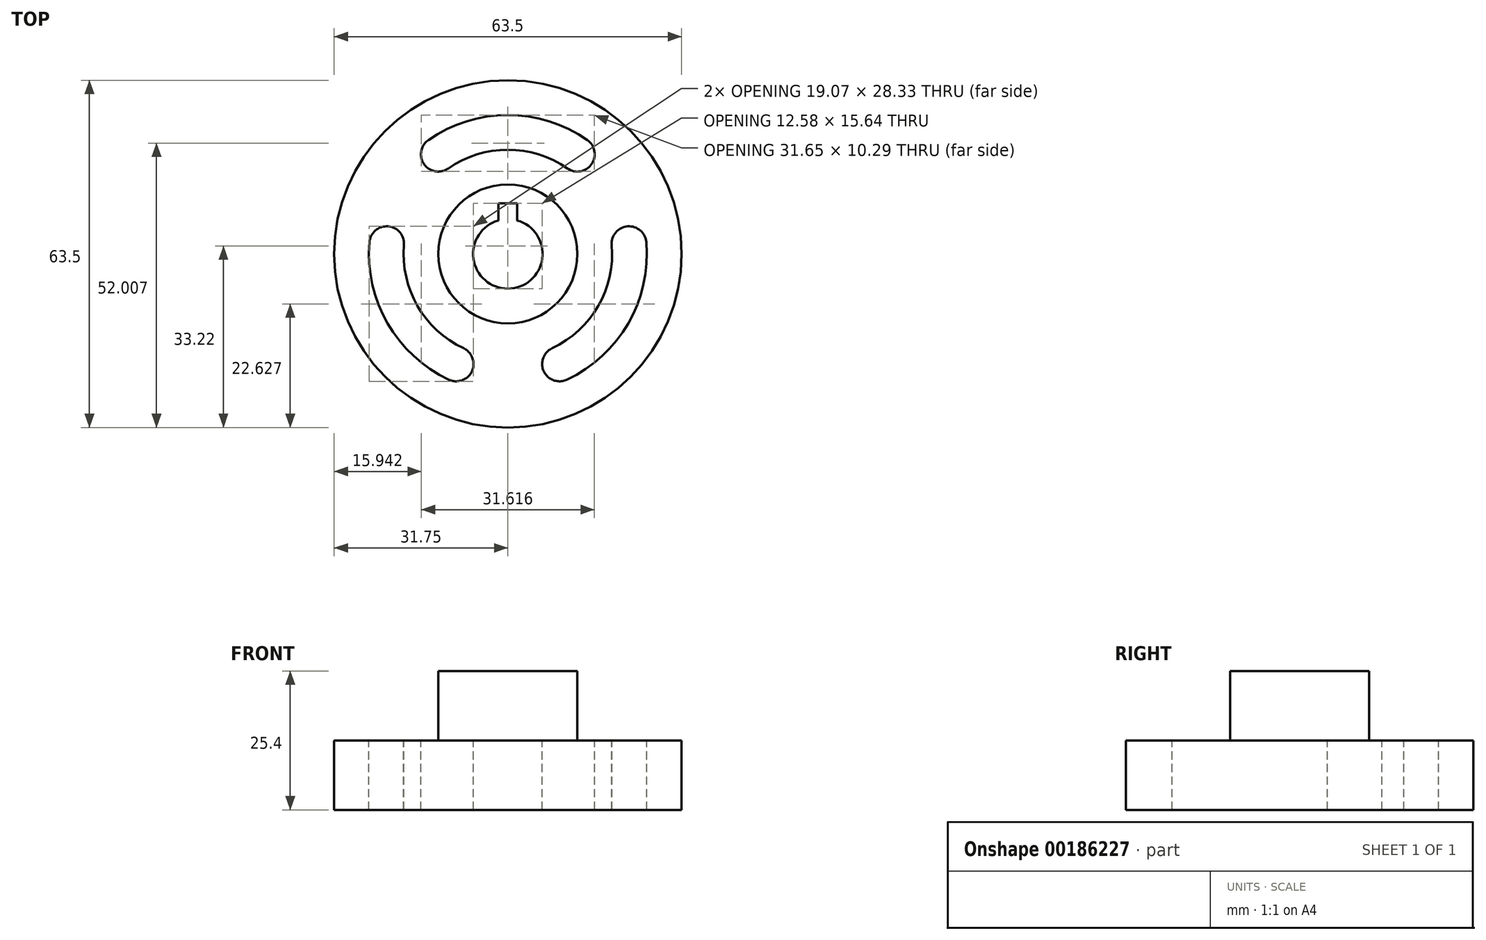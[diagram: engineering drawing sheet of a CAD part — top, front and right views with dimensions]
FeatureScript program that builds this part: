
annotation { "Feature Type Name" : "Feature", "Feature Type Description" : "" }
export const myFeature = defineFeature(function(context is Context, id is Id, definition is map)
    precondition{}
    {
        {
            var Q0;
            Q0=qCreatedBy(makeId("Top.planeOp"),FACE);
            var sketch = newSketch(context, id + "F0", { "sketchPlane" : qUnion([Q0])});
            skArc(sketch, "E0", {"start": v(-1.71, 6.11) * mm, "mid": v(0, -6.35) * mm, "end": v(1.71, 6.11) * mm});
            skCircle(sketch, "E1", {"center": v(0, 0) * mm, "radius": 12.7 * mm});
            skLineSegment(sketch, "E2.top", {"start": v(-1.71, 9.29) * mm, "end": v(1.71, 9.29) * mm});
            skLineSegment(sketch, "E2.left", {"start": v(-1.71, 6.11) * mm, "end": v(-1.71, 9.29) * mm});
            skLineSegment(sketch, "E2.right", {"start": v(1.71, 6.11) * mm, "end": v(1.71, 9.29) * mm});
            skLineSegment(sketch, "E3", {"start": v(0, 9.29) * mm, "end": v(0, 0) * mm, "construction": true});
            skSolve(sketch);
        }
        {
            var Q0;
            Q0=makeQuery(id+"F0.imprint","IMPRINT",FACE,{"disambiguationData":[TD([[makeQuery(id+"F0.imprint","IMPRINT",EDGE,{"derivedFrom":sQuery(id+"F0.wireOp",EDGE,"E0")}),-1.0]])]});
            extrude(context, id + "F1", {"entities" : qUnion([Q0]), "depth" : 25.4 * mm});
        }
        {
            var Q0;
            Q0=makeQuery(id+"F1.opExtrude","CAP_FACE",FACE,{"disambiguationData":[OSD([sQuery(id+"F0.wireOp",EDGE,"E0"),sQuery(id+"F0.wireOp",EDGE,"E1"),sQuery(id+"F0.wireOp",EDGE,"E2.top"),sQuery(id+"F0.wireOp",EDGE,"E2.left"),sQuery(id+"F0.wireOp",EDGE,"E2.right")])],"isStart":true});
            var sketch = newSketch(context, id + "F2", { "sketchPlane" : qUnion([Q0])});
            skCircle(sketch, "E4", {"center": v(0, 0) * mm, "radius": 31.75 * mm});
            skCircle(sketch, "E5.0", {"center": v(0, 0) * mm, "radius": 12.7 * mm});
            skSolve(sketch);
        }
        {
            var Q0;
            Q0=makeQuery(id+"F2.imprint","IMPRINT",FACE,{"disambiguationData":[TD([[makeQuery(id+"F2.imprint","IMPRINT",EDGE,{"derivedFrom":sQuery(id+"F2.wireOp",EDGE,"E4")}),1.0]])]});
            extrude(context, id + "F3", {"entities" : qUnion([Q0]), "operationType" : NewBodyOperationType.ADD, "oppositeDirection" : true, "depth" : 12.7 * mm});
        }
        {
            var Q0;
            Q0=makeQuery(id+"F3.opExtrude","CAP_FACE",FACE,{"disambiguationData":[OSD([sQuery(id+"F2.wireOp",EDGE,"E4"),sQuery(id+"F2.wireOp",EDGE,"E5.0")])],"isStart":false});
            var sketch = newSketch(context, id + "F4", { "sketchPlane" : qUnion([Q0])});
            skCircle(sketch, "E6.0", {"center": v(0, 0) * mm, "radius": 12.7 * mm, "construction": true});
            skLineSegment(sketch, "E7", {"start": v(0, 31.75) * mm, "end": v(0, 12.7) * mm, "construction": true});
            skLineSegment(sketch, "E8", {"start": v(0, -12.7) * mm, "end": v(0, -31.75) * mm});
            skArc(sketch, "E9", {"start": v(-12.7, 18.24) * mm, "mid": v(0, 22.23) * mm, "end": v(12.7, 18.24) * mm});
            skArc(sketch, "E10.0.startCap", {"start": v(-10.89, 15.63) * mm, "mid": v(-15.3, 16.42) * mm, "end": v(-14.51, 20.84) * mm});
            skArc(sketch, "E10.0.endCap", {"start": v(14.51, 20.84) * mm, "mid": v(15.3, 16.42) * mm, "end": v(10.89, 15.63) * mm});
            skArc(sketch, "E10.0.left", {"start": v(-14.51, 20.84) * mm, "mid": v(0, 25.4) * mm, "end": v(14.51, 20.84) * mm});
            skArc(sketch, "E10.0.right", {"start": v(-10.89, 15.63) * mm, "mid": v(0, 19.05) * mm, "end": v(10.89, 15.63) * mm});
            skLineSegment(sketch, "E11.1.0", {"start": v(-27.5, -15.88) * mm, "end": v(-11, -6.35) * mm, "construction": true});
            skArc(sketch, "E11.1.1", {"start": v(-9.45, -20.12) * mm, "mid": v(-19.25, -11.11) * mm, "end": v(-22.15, 1.88) * mm});
            skArc(sketch, "E11.1.2", {"start": v(-8.1, -17.24) * mm, "mid": v(-6.57, -21.47) * mm, "end": v(-10.8, -23) * mm});
            skArc(sketch, "E11.1.3", {"start": v(-25.3, 2.15) * mm, "mid": v(-21.88, 5.04) * mm, "end": v(-18.98, 1.61) * mm});
            skArc(sketch, "E11.1.4", {"start": v(-10.8, -23) * mm, "mid": v(-22, -12.7) * mm, "end": v(-25.3, 2.15) * mm});
            skArc(sketch, "E11.1.5", {"start": v(-8.1, -17.24) * mm, "mid": v(-16.5, -9.52) * mm, "end": v(-18.98, 1.61) * mm});
            skLineSegment(sketch, "E11.2.0", {"start": v(27.5, -15.88) * mm, "end": v(11, -6.35) * mm, "construction": true});
            skArc(sketch, "E11.2.1", {"start": v(22.15, 1.88) * mm, "mid": v(19.25, -11.11) * mm, "end": v(9.45, -20.12) * mm});
            skArc(sketch, "E11.2.2", {"start": v(18.98, 1.61) * mm, "mid": v(21.88, 5.04) * mm, "end": v(25.3, 2.15) * mm});
            skArc(sketch, "E11.2.3", {"start": v(10.8, -23) * mm, "mid": v(6.57, -21.47) * mm, "end": v(8.1, -17.24) * mm});
            skArc(sketch, "E11.2.4", {"start": v(25.3, 2.15) * mm, "mid": v(22, -12.7) * mm, "end": v(10.8, -23) * mm});
            skArc(sketch, "E11.2.5", {"start": v(18.98, 1.61) * mm, "mid": v(16.5, -9.53) * mm, "end": v(8.1, -17.24) * mm});
            skSolve(sketch);
        }
        {
            var Q0;
            Q0 = qSketchRegion(id + "F4", true);
            extrude(context, id + "F5", {"entities" : qUnion([Q0]), "operationType" : NewBodyOperationType.REMOVE, "oppositeDirection" : true, "depth" : 25.4 * mm});
        }
    });
